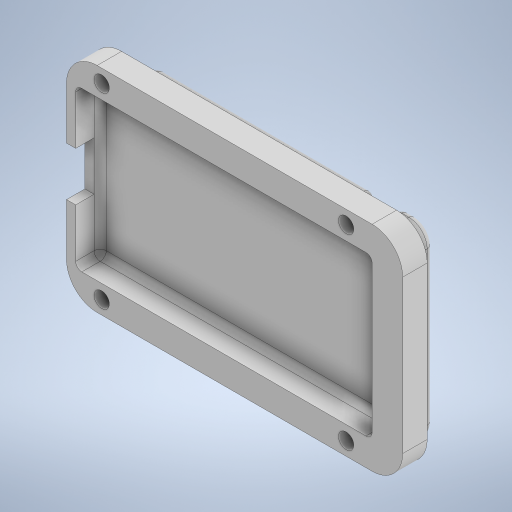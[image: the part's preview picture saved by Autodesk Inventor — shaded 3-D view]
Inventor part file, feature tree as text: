
AUTODESK INVENTOR PART (.ipt)
format: ipt  version: 2023 (Build 270158000, 158)  size: 401,920 bytes
history: native  units: mm
features: sketch x6, extrude x6, fillet x5, other x1, projected_geometry x1
ambient origin geometry x8: Origin, YZ Plane, XZ Plane, XY Plane, X Axis, Y Axis, Z Axis, Center Point
bodies: Body1 (feature_tree)
feature tree (19):
  other  "솔리드1"
  sketch  "스케치1"
  extrude  "돌출1"  Depth=35.0mm
  extrude  "돌출2"  Depth=58.5mm
  extrude  "돌출3"  Depth=48.5mm
  extrude  "돌출4"  Depth=26.0mm
  fillet  "모깎기1"  Radius=4.0mm
  sketch  "스케치4"
  extrude  "돌출5"  Depth=3.0mm TaperAngle=0.0deg
  fillet  "모깎기2"  Radius=2.5mm
  fillet  "모깎기3"  Radius=20.0mm
  extrude  "돌출6"  Depth=15.3mm
  fillet  "모깎기4"  Radius=6.0mm
  fillet  "모깎기5"  Radius=1.5mm
  sketch  "스케치2"
  sketch  "스케치3"
  sketch  "스케치5"
  projected_geometry  "투영된 루프1"
  sketch  "스케치6"
